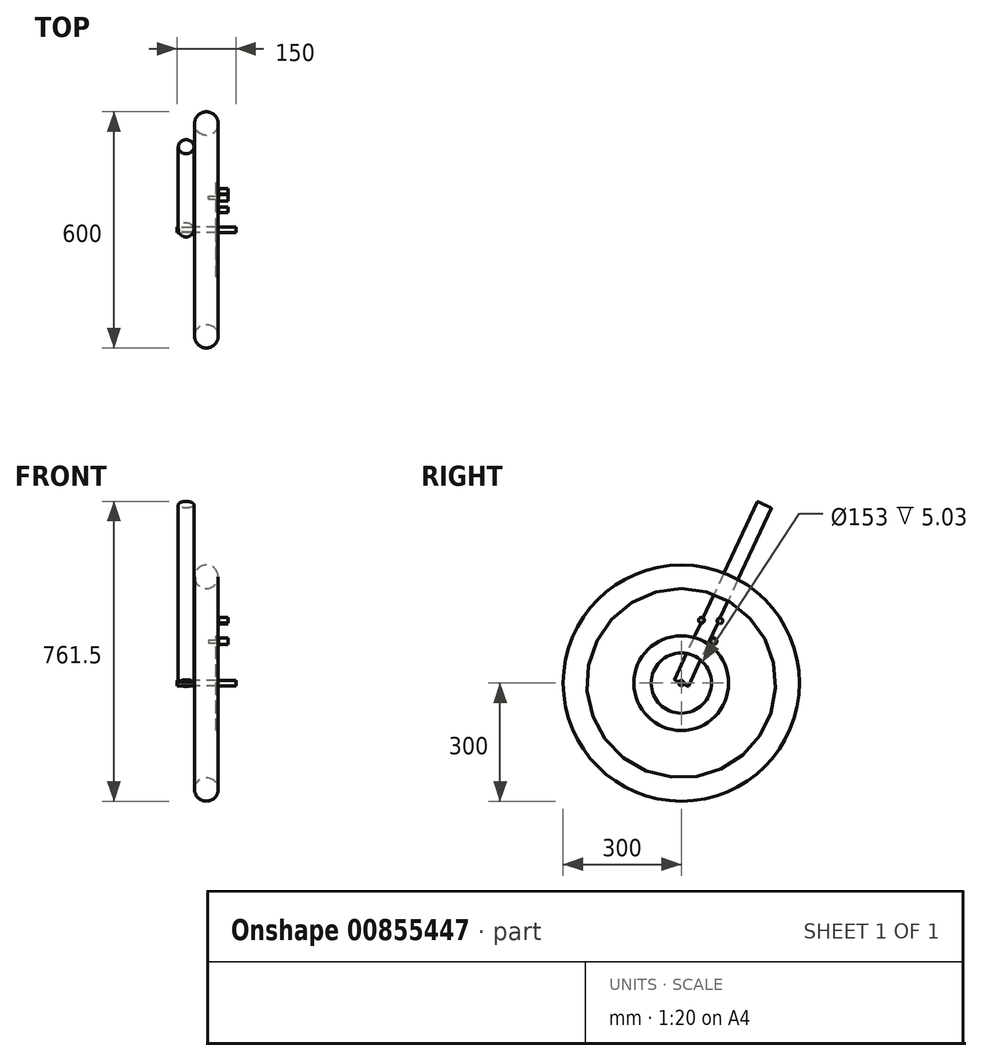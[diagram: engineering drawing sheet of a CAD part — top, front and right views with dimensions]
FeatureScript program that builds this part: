
annotation { "Feature Type Name" : "Feature", "Feature Type Description" : "" }
export const myFeature = defineFeature(function(context is Context, id is Id, definition is map)
    precondition{}
    {
        {
            var Q0;
            Q0=qCreatedBy(makeId("Front.planeOp"),FACE);
            var sketch = newSketch(context, id + "F0", { "sketchPlane" : qUnion([Q0])});
            skCircle(sketch, "E0", {"center": v(0, 270) * mm, "radius": 30 * mm});
            skLineSegment(sketch, "E1", {"start": v(-85.18, 0) * mm, "end": v(122.07, 0) * mm, "construction": true});
            skSolve(sketch);
        }
        {
            var Q0;
            Q0=makeQuery(id+"F0.imprint","IMPRINT",FACE,{"disambiguationData":[TD([[makeQuery(id+"F0.imprint","IMPRINT",EDGE,{"derivedFrom":sQuery(id+"F0.wireOp",EDGE,"E0")}),1.0]])]});
            var Q1;
            Q1=sQuery(id+"F0.wireOp",EDGE,"E1");
            revolve(context, id + "F1", {"surfaceOperationType" : NewSurfaceOperationType.NEW, "entities" : qUnion([Q0]), "axis" : qUnion([Q1]), "revolveType" : RevolveType.FULL});
        }
        {
            var Q0;
            Q0=qCreatedBy(makeId("Right.planeOp"),FACE);
            var sketch = newSketch(context, id + "F2", { "sketchPlane" : qUnion([Q0])});
            skCircle(sketch, "E2", {"center": v(0, 0) * mm, "radius": 6.72 * mm});
            skSolve(sketch);
        }
        {
            var Q0;
            Q0=makeQuery(id+"F2.imprint","IMPRINT",FACE,{"disambiguationData":[TD([[makeQuery(id+"F2.imprint","IMPRINT",EDGE,{"derivedFrom":sQuery(id+"F2.wireOp",EDGE,"E2")}),1.0]])]});
            extrude(context, id + "F3", {"entities" : qUnion([Q0]), "endBound" : BoundingType.SYMMETRIC, "depth" : 150 * mm, "offsetDistance" : 25 * mm, "hasSecondDirection" : true, "secondDirectionOppositeDirection" : true, "secondDirectionDepth" : 25 * mm});
        }
        {
            var Q0;
            Q0=qCreatedBy(makeId("Right.planeOp"),FACE);
            cPlane(context, id + "F4", {"entities" : qUnion([Q0]), "cplaneType" : CPlaneType.OFFSET, "offset" : 25 * mm, "width" : 150 * mm, "height" : 150 * mm});
        }
        {
            var Q0;
            Q0=qCreatedBy(id+"F4.planeOp",FACE);
            var sketch = newSketch(context, id + "F5", { "sketchPlane" : qUnion([Q0])});
            skCircle(sketch, "E3", {"center": v(0, 0) * mm, "radius": 120.25 * mm});
            skCircle(sketch, "E4", {"center": v(0, 0) * mm, "radius": 76.5 * mm});
            skSolve(sketch);
        }
        {
            var Q0;
            Q0=makeQuery(id+"F5.imprint","IMPRINT",FACE,{"disambiguationData":[TD([[makeQuery(id+"F5.imprint","IMPRINT",EDGE,{"derivedFrom":sQuery(id+"F5.wireOp",EDGE,"E3")}),1.0]])]});
            extrude(context, id + "F6", {"entities" : qUnion([Q0]), "depth" : 5.03 * mm, "offsetDistance" : 25 * mm});
        }
        {
            var Q0;
            Q0=qCreatedBy(makeId("Right.planeOp"),FACE);
            var sketch = newSketch(context, id + "F7", { "sketchPlane" : qUnion([Q0])});
            skLineSegment(sketch, "E5", {"start": v(0, 0) * mm, "end": v(107.43, 230.38) * mm, "construction": true});
            skLineSegment(sketch, "E6", {"start": v(0, 0) * mm, "end": v(0, 298.84) * mm, "construction": true});
            skSolve(sketch);
        }
        {
            var Q0;
            Q0=sQuery(id+"F7.wireOp",VERTEX,"E5.start");
            var Q1;
            Q1=sQuery(id+"F7.wireOp",EDGE,"E5");
            cPlane(context, id + "F8", {"entities" : qUnion([Q0, Q1]), "cplaneType" : CPlaneType.LINE_POINT, "offset" : 25 * mm, "width" : 150 * mm, "height" : 150 * mm});
        }
        {
            var Q0;
            Q0=qCreatedBy(id+"F8.planeOp",FACE);
            var sketch = newSketch(context, id + "F9", { "sketchPlane" : qUnion([Q0])});
            skCircle(sketch, "E7", {"center": v(-51.43, 0) * mm, "radius": 19.75 * mm});
            skLineSegment(sketch, "E8", {"start": v(0, 32.14) * mm, "end": v(0, -37.8) * mm, "construction": true});
            skCircle(sketch, "E9.MirrorC", {"center": v(51.43, 0) * mm, "radius": 19.75 * mm});
            skLineSegment(sketch, "E10.0", {"start": v(25, 120.25) * mm, "end": v(25, -120.25) * mm, "construction": true});
            skPoint(sketch, "E11", {"position": v(30.68, 0) * mm});
            skSolve(sketch);
        }
        {
            var Q0;
            Q0=makeQuery(id+"F9.imprint","IMPRINT",FACE,{"disambiguationData":[TD([[makeQuery(id+"F9.imprint","IMPRINT",EDGE,{"derivedFrom":sQuery(id+"F9.wireOp",EDGE,"E7")}),1.0]])]});
            var Q1;
            Q1=makeQuery(id+"F9.imprint","IMPRINT",FACE,{"disambiguationData":[TD([[makeQuery(id+"F9.imprint","IMPRINT",EDGE,{"derivedFrom":sQuery(id+"F9.wireOp",EDGE,"E9.MirrorC")}),-1.0]])]});
            extrude(context, id + "F10", {"entities" : qUnion([Q0, Q1]), "operationType" : NewBodyOperationType.ADD, "depth" : 500 * mm, "offsetDistance" : 25 * mm});
        }
        {
            var Q0;
            Q0=makeQuery(id+"F6.opExtrude","CAP_FACE",FACE,{"disambiguationData":[OSD([sQuery(id+"F5.wireOp",EDGE,"E3"),sQuery(id+"F5.wireOp",EDGE,"E4")])],"isStart":false});
            var Q1;
            Q1=sQuery(id+"F9.wireOp",VERTEX,"E11");
            cPlane(context, id + "F11", {"entities" : qUnion([Q0, Q1]), "cplaneType" : CPlaneType.PLANE_POINT, "offset" : 0 * mm, "width" : 150 * mm, "height" : 150 * mm});
        }
        {
            var Q0;
            Q0=qCreatedBy(id+"F11.planeOp",FACE);
            var sketch = newSketch(context, id + "F12", { "sketchPlane" : qUnion([Q0])});
            skLineSegment(sketch, "E12.0", {"start": v(0, 0) * mm, "end": v(107.43, 230.38) * mm, "construction": true});
            skCircle(sketch, "E13", {"center": v(81.72, 106.26) * mm, "radius": 8.6 * mm});
            skCircle(sketch, "E14", {"center": v(98.14, 158.05) * mm, "radius": 7.15 * mm});
            skCircle(sketch, "E15", {"center": v(51.34, 159.62) * mm, "radius": 7.2 * mm});
            skCircle(sketch, "E16.0", {"center": v(0, 0) * mm, "radius": 120.25 * mm});
            skLineSegment(sketch, "E17", {"start": v(0, 0) * mm, "end": v(105.35, 137) * mm, "construction": true});
            skPoint(sketch, "E18", {"position": v(79.34, 103.17) * mm});
            skLineSegment(sketch, "E19", {"start": v(-17.9, 8.35) * mm, "end": v(193.4, 461.5) * mm, "construction": true});
            skLineSegment(sketch, "E20", {"start": v(229.2, 444.8) * mm, "end": v(17.9, -8.35) * mm, "construction": true});
            skSolve(sketch);
        }
        {
            var Q0;
            Q0=makeQuery(id+"F12.imprint","IMPRINT",FACE,{"disambiguationData":[TD([[makeQuery(id+"F12.imprint","IMPRINT",EDGE,{"derivedFrom":sQuery(id+"F12.wireOp",EDGE,"E14")}),1.0]])]});
            var Q1;
            Q1=makeQuery(id+"F12.imprint","IMPRINT",FACE,{"disambiguationData":[TD([[makeQuery(id+"F12.imprint","IMPRINT",EDGE,{"derivedFrom":sQuery(id+"F12.wireOp",EDGE,"E13")}),1.0]])]});
            var Q2;
            Q2=makeQuery(id+"F12.imprint","IMPRINT",FACE,{"disambiguationData":[TD([[makeQuery(id+"F12.imprint","IMPRINT",EDGE,{"derivedFrom":sQuery(id+"F12.wireOp",EDGE,"E15")}),1.0]])]});
            extrude(context, id + "F13", {"entities" : qUnion([Q0, Q1, Q2]), "depth" : 25 * mm, "hasOffset" : true, "offsetDistance" : 25 * mm});
        }
        {
            var Q0;
            Q0=makeQuery(id+"F13.opExtrude","CAP_FACE",FACE,{"disambiguationData":[OSD([sQuery(id+"F12.wireOp",EDGE,"E13")])],"isStart":true});
            var sketch = newSketch(context, id + "F14", { "sketchPlane" : qUnion([Q0])});
            skCircle(sketch, "E21", {"center": v(-81.72, 106.26) * mm, "radius": 3.9 * mm});
            skLineSegment(sketch, "E22.0", {"start": v(0, 0) * mm, "end": v(-105.35, 137) * mm});
            skCircle(sketch, "E22.1", {"center": v(0, 0) * mm, "radius": 120.25 * mm});
            skPoint(sketch, "E23", {"position": v(-73.3, 95.32) * mm});
            skCircle(sketch, "E24.0", {"center": v(-81.72, 106.26) * mm, "radius": 8.6 * mm});
            skSolve(sketch);
        }
        {
            var Q0;
            Q0=makeQuery(id+"F14.imprint","IMPRINT",FACE,{"disambiguationData":[TD([[makeQuery(id+"F14.imprint","IMPRINT",EDGE,{"derivedFrom":sQuery(id+"F14.wireOp",EDGE,"E21")}),1.0]])]});
            extrude(context, id + "F15", {"entities" : qUnion([Q0]), "operationType" : NewBodyOperationType.ADD, "depth" : 25.4 * mm, "offsetDistance" : 25 * mm});
        }
    });
